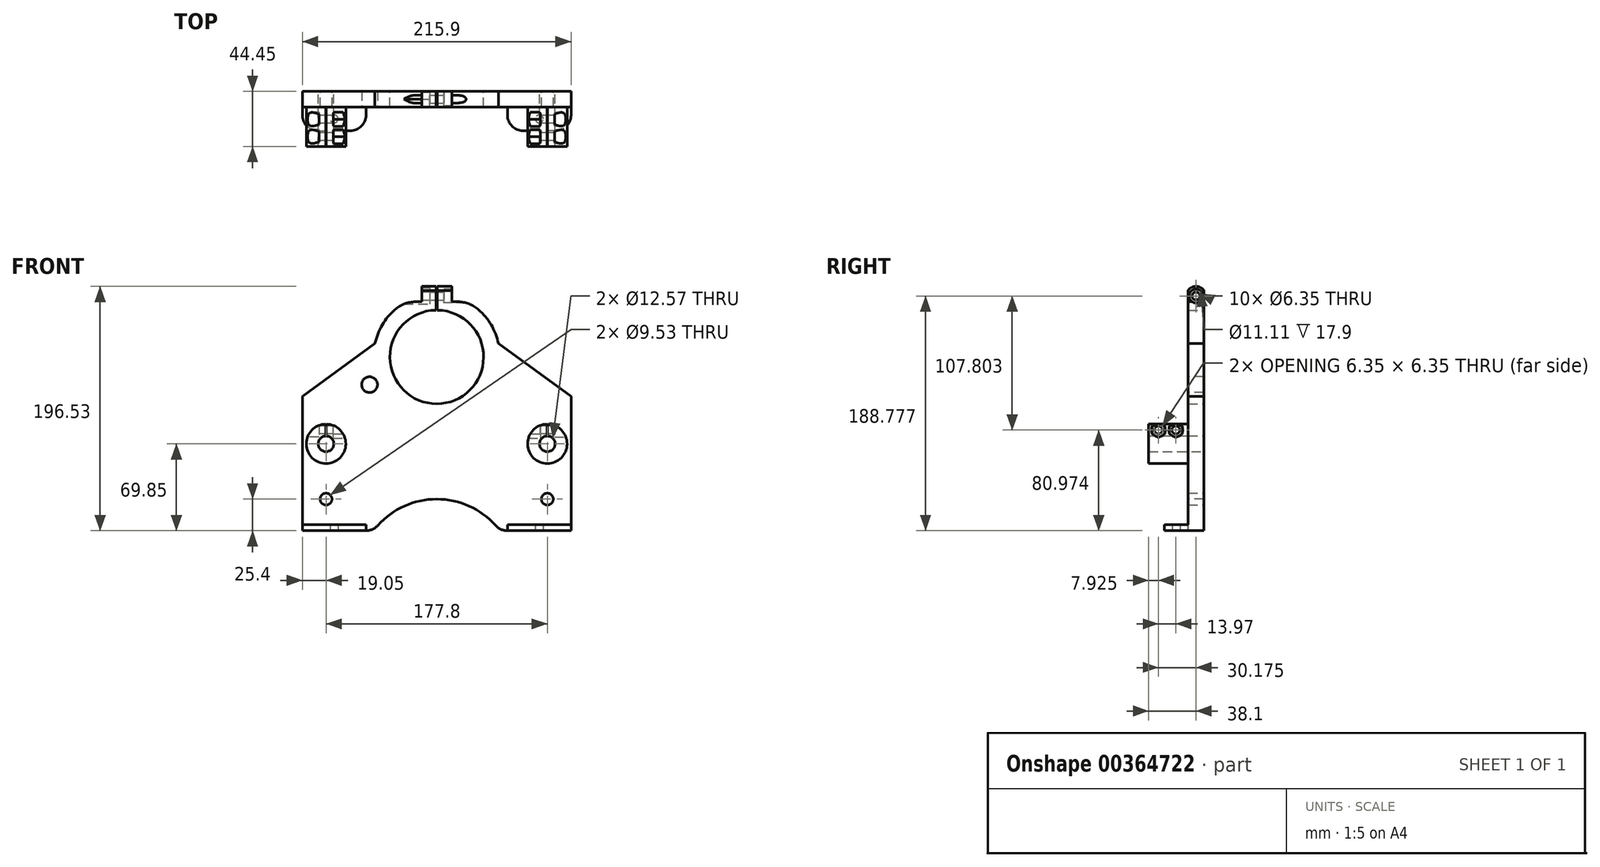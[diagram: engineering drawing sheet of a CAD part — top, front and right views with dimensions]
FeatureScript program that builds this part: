
annotation { "Feature Type Name" : "Feature", "Feature Type Description" : "" }
export const myFeature = defineFeature(function(context is Context, id is Id, definition is map)
    precondition{}
    {
        {
            var Q0;
            Q0=qCreatedBy(makeId("Front.planeOp"),FACE);
            var sketch = newSketch(context, id + "F0", { "sketchPlane" : qUnion([Q0])});
            skCircle(sketch, "E0", {"center": v(-88.9, 0) * mm, "radius": 6.29 * mm});
            skCircle(sketch, "E1", {"center": v(88.9, 0) * mm, "radius": 6.29 * mm});
            skCircle(sketch, "E2", {"center": v(-88.9, -44.45) * mm, "radius": 4.76 * mm});
            skCircle(sketch, "E3", {"center": v(88.9, -44.45) * mm, "radius": 4.76 * mm});
            skLineSegment(sketch, "E4.top", {"start": v(-107.95, -69.85) * mm, "end": v(107.95, -69.85) * mm});
            skLineSegment(sketch, "E4.left", {"start": v(-107.95, 38.1) * mm, "end": v(-107.95, -69.85) * mm});
            skLineSegment(sketch, "E4.right", {"start": v(107.95, 38.1) * mm, "end": v(107.95, -69.85) * mm});
            skPoint(sketch, "E4.middle", {"position": v(0, -15.87) * mm});
            skCircle(sketch, "E5", {"center": v(0, 69.85) * mm, "radius": 37.66 * mm});
            skArc(sketch, "E6", {"start": v(22.5, 100.6) * mm, "mid": v(0, 107.95) * mm, "end": v(-22.5, 100.6) * mm});
            skLineSegment(sketch, "E7", {"start": v(-107.95, 38.1) * mm, "end": v(-22.5, 100.6) * mm});
            skLineSegment(sketch, "E8", {"start": v(107.95, 38.1) * mm, "end": v(22.5, 100.6) * mm});
            skPoint(sketch, "E9.center.orphan", {"position": v(0, 0) * mm});
            skSolve(sketch);
        }
        {
            var Q0;
            Q0=qSketchRegion(id+"F0",true);
            extrude(context, id + "F1", {"entities" : qUnion([Q0]), "depth" : 12.7 * mm});
        }
        {
            var Q0;
            Q0=makeQuery(id+"F1.opExtrude","CAP_FACE",FACE,{"disambiguationData":[OSD([sQuery(id+"F0.wireOp",EDGE,"E9"),sQuery(id+"F0.wireOp",EDGE,"E0"),sQuery(id+"F0.wireOp",EDGE,"E1"),sQuery(id+"F0.wireOp",EDGE,"E2"),sQuery(id+"F0.wireOp",EDGE,"E3"),sQuery(id+"F0.wireOp",EDGE,"E4.bottom"),sQuery(id+"F0.wireOp",EDGE,"E4.top"),sQuery(id+"F0.wireOp",EDGE,"E4.left"),sQuery(id+"F0.wireOp",EDGE,"E4.right")])],"isStart":false});
            var sketch = newSketch(context, id + "F2", { "sketchPlane" : qUnion([Q0])});
            skCircle(sketch, "E10", {"center": v(0, -107.95) * mm, "radius": 63.5 * mm});
            skSolve(sketch);
        }
        {
            var Q0;
            Q0=qSketchRegion(id+"F2",true);
            extrude(context, id + "F3", {"entities" : qUnion([Q0]), "operationType" : NewBodyOperationType.REMOVE, "oppositeDirection" : true, "depth" : 25.4 * mm});
        }
        {
            var Q0;
            Q0=makeQuery(id+"F3.boolean.opBoolean","INTERSECT",EDGE,{"disambiguationData":[OD(0.0)],"derivedFrom":[makeQuery(id+"F1.opExtrude","SWEPT_FACE",FACE,{"disambiguationData":[OSD([sQuery(id+"F0.wireOp",EDGE,"E4.top")])]}),makeQuery(id+"F3.opExtrude","SWEPT_FACE",FACE,{"disambiguationData":[OSD([sQuery(id+"F2.wireOp",EDGE,"E10")])]})]});
            var Q1;
            Q1=makeQuery(id+"F3.boolean.opBoolean","INTERSECT",EDGE,{"disambiguationData":[OD(1.0)],"derivedFrom":[makeQuery(id+"F1.opExtrude","SWEPT_FACE",FACE,{"disambiguationData":[OSD([sQuery(id+"F0.wireOp",EDGE,"E4.top")])]}),makeQuery(id+"F3.opExtrude","SWEPT_FACE",FACE,{"disambiguationData":[OSD([sQuery(id+"F2.wireOp",EDGE,"E10")])]})]});
            fillet(context, id + "F4", {"entities" : qUnion([Q0, Q1]), "radius" : 12.7 * mm, "tangentPropagation" : true, "allowEdgeOverflow" : false});
        }
        {
            var Q0;
            Q0=makeQuery(id+"F1.opExtrude","CAP_FACE",FACE,{"disambiguationData":[OSD([sQuery(id+"F0.wireOp",EDGE,"E9"),sQuery(id+"F0.wireOp",EDGE,"E0"),sQuery(id+"F0.wireOp",EDGE,"E1"),sQuery(id+"F0.wireOp",EDGE,"E2"),sQuery(id+"F0.wireOp",EDGE,"E3"),sQuery(id+"F0.wireOp",EDGE,"E4.bottom"),sQuery(id+"F0.wireOp",EDGE,"E4.top"),sQuery(id+"F0.wireOp",EDGE,"E4.left"),sQuery(id+"F0.wireOp",EDGE,"E4.right")])],"isStart":false});
            var sketch = newSketch(context, id + "F5", { "sketchPlane" : qUnion([Q0])});
            skCircle(sketch, "E11.0", {"center": v(-88.9, 0) * mm, "radius": 6.29 * mm});
            skCircle(sketch, "E12", {"center": v(-88.9, 0) * mm, "radius": 15.88 * mm});
            skCircle(sketch, "E13.0", {"center": v(88.9, 0) * mm, "radius": 6.29 * mm});
            skCircle(sketch, "E14", {"center": v(88.9, 0) * mm, "radius": 15.88 * mm});
            skSolve(sketch);
        }
        {
            var Q0;
            Q0=qSketchRegion(id+"F5",true);
            extrude(context, id + "F6", {"entities" : qUnion([Q0]), "operationType" : NewBodyOperationType.ADD, "depth" : 31.75 * mm});
        }
        {
            var Q0;
            Q0=makeQuery(id+"F6.opExtrude","CAP_FACE",FACE,{"disambiguationData":[OSD([sQuery(id+"F5.wireOp",EDGE,"E11.0"),sQuery(id+"F5.wireOp",EDGE,"E12")])],"isStart":false});
            var sketch = newSketch(context, id + "F7", { "sketchPlane" : qUnion([Q0])});
            skLineSegment(sketch, "E15.bottom", {"start": v(-89.1, 1.72) * mm, "end": v(-88.7, 1.72) * mm});
            skLineSegment(sketch, "E15.top", {"start": v(-89.1, 19.66) * mm, "end": v(-88.7, 19.66) * mm});
            skLineSegment(sketch, "E15.left", {"start": v(-89.1, 1.72) * mm, "end": v(-89.1, 19.66) * mm});
            skLineSegment(sketch, "E15.right", {"start": v(-88.7, 1.72) * mm, "end": v(-88.7, 19.66) * mm});
            skLineSegment(sketch, "E16", {"start": v(-88.9, 1.72) * mm, "end": v(-88.9, 0) * mm});
            skPoint(sketch, "E16.endSnap0", {"position": v(-88.9, 1.72) * mm});
            skLineSegment(sketch, "E17.bottom", {"start": v(88.7, 20.83) * mm, "end": v(89.1, 20.83) * mm});
            skLineSegment(sketch, "E17.top", {"start": v(88.7, 3.08) * mm, "end": v(89.1, 3.08) * mm});
            skLineSegment(sketch, "E17.left", {"start": v(88.7, 20.83) * mm, "end": v(88.7, 3.08) * mm});
            skLineSegment(sketch, "E17.right", {"start": v(89.1, 20.83) * mm, "end": v(89.1, 3.08) * mm});
            skLineSegment(sketch, "E18", {"start": v(88.9, 0) * mm, "end": v(88.9, 3.08) * mm});
            skSolve(sketch);
        }
        {
            var Q0;
            Q0=qSketchRegion(id+"F7",true);
            var Q1;
            Q1=makeQuery(id+"F1.opExtrude","CAP_FACE",FACE,{"disambiguationData":[OSD([sQuery(id+"F0.wireOp",EDGE,"E9"),sQuery(id+"F0.wireOp",EDGE,"E0"),sQuery(id+"F0.wireOp",EDGE,"E1"),sQuery(id+"F0.wireOp",EDGE,"E2"),sQuery(id+"F0.wireOp",EDGE,"E3"),sQuery(id+"F0.wireOp",EDGE,"E4.bottom"),sQuery(id+"F0.wireOp",EDGE,"E4.top"),sQuery(id+"F0.wireOp",EDGE,"E4.left"),sQuery(id+"F0.wireOp",EDGE,"E4.right")])],"isStart":false});
            extrude(context, id + "F8", {"entities" : qUnion([Q0]), "operationType" : NewBodyOperationType.REMOVE, "endBound" : BoundingType.UP_TO_SURFACE, "oppositeDirection" : true, "endBoundEntityFace" : qUnion([Q1]), "depth" : 25.4 * mm});
        }
        {
            var Q0;
            Q0=makeQuery(id+"F1.opExtrude","SWEPT_FACE",FACE,{"disambiguationData":[OSD([sQuery(id+"F0.wireOp",EDGE,"E4.left")])]});
            var sketch = newSketch(context, id + "F9", { "sketchPlane" : qUnion([Q0])});
            skCircle(sketch, "E19", {"center": v(36.53, 11.12) * mm, "radius": 3.18 * mm});
            skCircle(sketch, "E20", {"center": v(22.56, 11.12) * mm, "radius": 3.18 * mm});
            skSolve(sketch);
        }
        {
            var Q0;
            Q0=qSketchRegion(id+"F9",true);
            extrude(context, id + "F10", {"entities" : qUnion([Q0]), "operationType" : NewBodyOperationType.REMOVE, "oppositeDirection" : true, "depth" : 224.54 * mm});
        }
        {
            var Q0;
            Q0=qCreatedBy(makeId("Right.planeOp"),FACE);
            var sketch = newSketch(context, id + "F11", { "sketchPlane" : qUnion([Q0])});
            skCircle(sketch, "E21.0", {"center": v(-36.53, 11.12) * mm, "radius": 3.18 * mm, "construction": true});
            skCircle(sketch, "E22.0", {"center": v(-22.56, 11.12) * mm, "radius": 3.18 * mm, "construction": true});
            skCircle(sketch, "E23.cCircle", {"center": v(-36.53, 11.12) * mm, "radius": 6.48 * mm, "construction": true});
            skLineSegment(sketch, "E23.0", {"start": v(-36.53, 17.6) * mm, "end": v(-30.92, 14.36) * mm});
            skLineSegment(sketch, "E23.1", {"start": v(-30.92, 14.36) * mm, "end": v(-30.92, 7.89) * mm});
            skLineSegment(sketch, "E23.2", {"start": v(-30.92, 7.89) * mm, "end": v(-36.53, 4.65) * mm});
            skLineSegment(sketch, "E23.3", {"start": v(-36.53, 4.65) * mm, "end": v(-42.13, 7.89) * mm});
            skLineSegment(sketch, "E23.4", {"start": v(-42.13, 7.89) * mm, "end": v(-42.13, 14.36) * mm});
            skLineSegment(sketch, "E23.5", {"start": v(-42.13, 14.36) * mm, "end": v(-36.53, 17.6) * mm});
            skCircle(sketch, "E24.cCircle", {"center": v(-22.56, 11.12) * mm, "radius": 6.48 * mm, "construction": true});
            skLineSegment(sketch, "E24.0", {"start": v(-28.16, 14.36) * mm, "end": v(-22.56, 17.6) * mm});
            skLineSegment(sketch, "E24.1", {"start": v(-22.56, 17.6) * mm, "end": v(-16.95, 14.36) * mm});
            skLineSegment(sketch, "E24.2", {"start": v(-16.95, 14.36) * mm, "end": v(-16.95, 7.89) * mm});
            skLineSegment(sketch, "E24.3", {"start": v(-16.95, 7.89) * mm, "end": v(-22.56, 4.65) * mm});
            skLineSegment(sketch, "E24.4", {"start": v(-22.56, 4.65) * mm, "end": v(-28.16, 7.89) * mm});
            skLineSegment(sketch, "E24.5", {"start": v(-28.16, 7.89) * mm, "end": v(-28.16, 14.36) * mm});
            skSolve(sketch);
        }
        {
            var Q0;
            Q0=makeQuery(id+"F11.imprint","IMPRINT",FACE,{"disambiguationData":[TD([[makeQuery(id+"F11.imprint","IMPRINT",EDGE,{"derivedFrom":sQuery(id+"F11.wireOp",EDGE,"E23.0")}),-1.0]])]});
            var Q1;
            Q1=makeQuery(id+"F11.imprint","IMPRINT",FACE,{"disambiguationData":[TD([[makeQuery(id+"F11.imprint","IMPRINT",EDGE,{"derivedFrom":sQuery(id+"F11.wireOp",EDGE,"E24.0")}),-1.0]])]});
            var Q2;
            Q2=sQuery(id+"F11.wireOp",EDGE,"E21.0");
            var Q3;
            Q3=sQuery(id+"F11.wireOp",EDGE,"E22.0");
            extrude(context, id + "F12", {"entities" : qUnion([Q0, Q1]), "operationType" : NewBodyOperationType.REMOVE, "surfaceEntities" : qUnion([Q2, Q3]), "oppositeDirection" : true, "depth" : 83.18 * mm, "hasSecondDirection" : true, "secondDirectionOppositeDirection" : false, "secondDirectionDepth" : 83.18 * mm});
        }
        {
            var Q0;
            Q0=makeQuery(id+"F1.opExtrude","SWEPT_FACE",FACE,{"disambiguationData":[OSD([sQuery(id+"F0.wireOp",EDGE,"E4.left")])]});
            var sketch = newSketch(context, id + "F13", { "sketchPlane" : qUnion([Q0])});
            skCircle(sketch, "E25.0", {"center": v(36.53, 11.12) * mm, "radius": 3.18 * mm, "construction": true});
            skCircle(sketch, "E26.0", {"center": v(22.56, 11.12) * mm, "radius": 3.18 * mm, "construction": true});
            skCircle(sketch, "E27", {"center": v(22.56, 11.12) * mm, "radius": 5.56 * mm});
            skCircle(sketch, "E28", {"center": v(36.53, 11.12) * mm, "radius": 5.56 * mm});
            skSolve(sketch);
        }
        {
            var Q0;
            Q0=qSketchRegion(id+"F13",true);
            extrude(context, id + "F14", {"entities" : qUnion([Q0]), "operationType" : NewBodyOperationType.REMOVE, "oppositeDirection" : true, "depth" : 13.33 * mm});
        }
        {
            var Q0;
            Q0=makeQuery(id+"F1.opExtrude","SWEPT_FACE",FACE,{"disambiguationData":[OSD([sQuery(id+"F0.wireOp",EDGE,"E4.right")])]});
            var sketch = newSketch(context, id + "F15", { "sketchPlane" : qUnion([Q0])});
            skCircle(sketch, "E29.0", {"center": v(-36.53, 11.12) * mm, "radius": 3.18 * mm, "construction": true});
            skCircle(sketch, "E29.1", {"center": v(-22.56, 11.12) * mm, "radius": 3.18 * mm, "construction": true});
            skCircle(sketch, "E30", {"center": v(-36.53, 11.12) * mm, "radius": 5.56 * mm});
            skCircle(sketch, "E31", {"center": v(-22.56, 11.12) * mm, "radius": 5.56 * mm});
            skSolve(sketch);
        }
        {
            var Q0;
            Q0=qSketchRegion(id+"F15",true);
            extrude(context, id + "F16", {"entities" : qUnion([Q0]), "operationType" : NewBodyOperationType.REMOVE, "oppositeDirection" : true, "depth" : 13.33 * mm});
        }
        {
            var Q0;
            {var subQ1=sQuery(id+"F0.wireOp",EDGE,"E4.left");var subQ2=sQuery(id+"F0.wireOp",EDGE,"E4.top");Q0=makeQuery(id+"F3.boolean.opBoolean","SPLIT",FACE,{"disambiguationData":[TD([makeQuery(id+"F1.opExtrude","SWEPT_FACE",FACE,{"disambiguationData":[OSD([subQ1])]})])],"derivedFrom":makeQuery(id+"F1.opExtrude","SWEPT_FACE",FACE,{"disambiguationData":[OSD([subQ2])]})});}
            var sketch = newSketch(context, id + "F17", { "sketchPlane" : qUnion([Q0])});
            skLineSegment(sketch, "E32.0", {"start": v(56.8, 12.7) * mm, "end": v(107.95, 12.7) * mm});
            skLineSegment(sketch, "E33", {"start": v(107.95, 12.7) * mm, "end": v(107.95, 31.75) * mm});
            skLineSegment(sketch, "E34", {"start": v(107.95, 31.75) * mm, "end": v(56.8, 31.75) * mm});
            skLineSegment(sketch, "E35", {"start": v(56.8, 31.75) * mm, "end": v(56.8, 12.7) * mm});
            skCircle(sketch, "E36", {"center": v(82.37, 22.23) * mm, "radius": 3.18 * mm});
            skLineSegment(sketch, "E37", {"start": v(107.95, 22.23) * mm, "end": v(56.8, 22.23) * mm, "construction": true});
            skLineSegment(sketch, "E38.bottom", {"start": v(-107.95, 12.7) * mm, "end": v(-56.8, 12.7) * mm});
            skLineSegment(sketch, "E38.top", {"start": v(-107.95, 31.75) * mm, "end": v(-56.8, 31.75) * mm});
            skLineSegment(sketch, "E38.left", {"start": v(-107.95, 12.7) * mm, "end": v(-107.95, 31.75) * mm});
            skLineSegment(sketch, "E38.right", {"start": v(-56.8, 12.7) * mm, "end": v(-56.8, 31.75) * mm});
            skCircle(sketch, "E39", {"center": v(-82.37, 22.22) * mm, "radius": 3.18 * mm});
            skPoint(sketch, "E39.centerSnap0", {"position": v(-82.37, 31.75) * mm});
            skSolve(sketch);
        }
        {
            var Q0;
            Q0=qSketchRegion(id+"F17",true);
            extrude(context, id + "F18", {"entities" : qUnion([Q0]), "operationType" : NewBodyOperationType.ADD, "oppositeDirection" : true, "depth" : 4.75 * mm});
        }
        {
            var Q0;
            Q0=makeQuery(id+"F18.opExtrude","SWEPT_EDGE",EDGE,{"disambiguationData":[OSD([sQuery(id+"F17.wireOp",EDGE,"E34"),sQuery(id+"F17.wireOp",EDGE,"E35")])]});
            var Q1;
            Q1=makeQuery(id+"F18.opExtrude","SWEPT_EDGE",EDGE,{"disambiguationData":[OSD([sQuery(id+"F17.wireOp",EDGE,"E33"),sQuery(id+"F17.wireOp",EDGE,"E34")])]});
            var Q2;
            Q2=makeQuery(id+"F18.opExtrude","SWEPT_EDGE",EDGE,{"disambiguationData":[OSD([sQuery(id+"F17.wireOp",EDGE,"E38.top"),sQuery(id+"F17.wireOp",EDGE,"E38.right")])]});
            var Q3;
            Q3=makeQuery(id+"F18.opExtrude","SWEPT_EDGE",EDGE,{"disambiguationData":[OSD([sQuery(id+"F17.wireOp",EDGE,"E38.top"),sQuery(id+"F17.wireOp",EDGE,"E38.left")])]});
            fillet(context, id + "F19", {"entities" : qUnion([Q0, Q1, Q2, Q3]), "radius" : 12.7 * mm, "tangentPropagation" : true, "allowEdgeOverflow" : false});
        }
        {
            var Q0;
            {var subQ0=sQuery(id+"F0.wireOp",EDGE,"E8");var subQ1=sQuery(id+"F0.wireOp",EDGE,"E7");var subQ2=sQuery(id+"F0.wireOp",EDGE,"E6");var subQ3=sQuery(id+"F0.wireOp",EDGE,"E5");var subQ4=sQuery(id+"F0.wireOp",EDGE,"E4.right");var subQ5=sQuery(id+"F0.wireOp",EDGE,"E4.left");var subQ6=sQuery(id+"F0.wireOp",EDGE,"E4.top");var subQ7=sQuery(id+"F0.wireOp",EDGE,"E3");var subQ8=sQuery(id+"F0.wireOp",EDGE,"E2");var subQ9=sQuery(id+"F0.wireOp",EDGE,"E1");var subQ10=sQuery(id+"F0.wireOp",EDGE,"E0");var subQ11=sQuery(id+"F7.wireOp",EDGE,"E15.bottom");Q0=makeQuery(id+"F8.boolean.opBoolean","MERGE",FACE,{"derivedFrom":[makeQuery(id+"F1.opExtrude","CAP_FACE",FACE,{"disambiguationData":[OSD([subQ10,subQ9,subQ8,subQ7,subQ6,subQ5,subQ4,subQ3,subQ2,subQ1,subQ0])],"isStart":false}),makeQuery(id+"F8.opExtrude","CAP_FACE",FACE,{"disambiguationData":[OSD([subQ10,subQ9,subQ8,subQ7,subQ6,subQ5,subQ4,subQ3,subQ2,subQ1,subQ0]),ownerDisambiguation([makeQuery(id+"F7.imprint","IMPRINT",EDGE,{"disambiguationData":[TD([[makeQuery(id+"F7.imprint","IMPRINT",VERTEX,{"derivedFrom":subQ11}),1.0]])],"derivedFrom":subQ11})])],"isStart":false}),makeQuery(id+"F8.opExtrude","CAP_FACE",FACE,{"disambiguationData":[OSD([subQ10,subQ9,subQ8,subQ7,subQ6,subQ5,subQ4,subQ3,subQ2,subQ1,subQ0]),ownerDisambiguation([makeQuery(id+"F7.imprint","IMPRINT",EDGE,{"derivedFrom":sQuery(id+"F7.wireOp",EDGE,"E17.bottom")})])],"isStart":false})]});}
            var sketch = newSketch(context, id + "F20", { "sketchPlane" : qUnion([Q0])});
            skCircle(sketch, "E40", {"center": v(0, 69.85) * mm, "radius": 50.8 * mm});
            skCircle(sketch, "E41.0", {"center": v(0, 69.85) * mm, "radius": 37.66 * mm});
            skSolve(sketch);
        }
        {
            var Q0;
            Q0=qSketchRegion(id+"F20",true);
            extrude(context, id + "F21", {"entities" : qUnion([Q0]), "operationType" : NewBodyOperationType.ADD, "oppositeDirection" : true, "depth" : 12.7 * mm});
        }
        {
            var Q0;
            {var subQ0=sQuery(id+"F0.wireOp",EDGE,"E8");var subQ1=sQuery(id+"F0.wireOp",EDGE,"E7");var subQ2=sQuery(id+"F0.wireOp",EDGE,"E6");var subQ3=sQuery(id+"F0.wireOp",EDGE,"E5");var subQ4=sQuery(id+"F0.wireOp",EDGE,"E4.right");var subQ5=sQuery(id+"F0.wireOp",EDGE,"E4.left");var subQ6=sQuery(id+"F0.wireOp",EDGE,"E4.top");var subQ7=sQuery(id+"F0.wireOp",EDGE,"E3");var subQ8=sQuery(id+"F0.wireOp",EDGE,"E2");var subQ9=sQuery(id+"F0.wireOp",EDGE,"E1");var subQ10=sQuery(id+"F0.wireOp",EDGE,"E0");var subQ11=sQuery(id+"F7.wireOp",EDGE,"E15.bottom");Q0=makeQuery(id+"F21.boolean.opBoolean","MERGE",FACE,{"derivedFrom":[makeQuery(id+"F8.boolean.opBoolean","MERGE",FACE,{"derivedFrom":[makeQuery(id+"F1.opExtrude","CAP_FACE",FACE,{"disambiguationData":[OSD([subQ10,subQ9,subQ8,subQ7,subQ6,subQ5,subQ4,subQ3,subQ2,subQ1,subQ0])],"isStart":false}),makeQuery(id+"F8.opExtrude","CAP_FACE",FACE,{"disambiguationData":[OSD([subQ10,subQ9,subQ8,subQ7,subQ6,subQ5,subQ4,subQ3,subQ2,subQ1,subQ0]),ownerDisambiguation([makeQuery(id+"F7.imprint","IMPRINT",EDGE,{"disambiguationData":[TD([[makeQuery(id+"F7.imprint","IMPRINT",VERTEX,{"derivedFrom":subQ11}),1.0]])],"derivedFrom":subQ11})])],"isStart":false}),makeQuery(id+"F8.opExtrude","CAP_FACE",FACE,{"disambiguationData":[OSD([subQ10,subQ9,subQ8,subQ7,subQ6,subQ5,subQ4,subQ3,subQ2,subQ1,subQ0]),ownerDisambiguation([makeQuery(id+"F7.imprint","IMPRINT",EDGE,{"derivedFrom":sQuery(id+"F7.wireOp",EDGE,"E17.bottom")})])],"isStart":false})]}),makeQuery(id+"F21.opExtrude","CAP_FACE",FACE,{"disambiguationData":[OSD([sQuery(id+"F20.wireOp",EDGE,"E40"),sQuery(id+"F20.wireOp",EDGE,"E41.0")])],"isStart":true})]});}
            var sketch = newSketch(context, id + "F22", { "sketchPlane" : qUnion([Q0])});
            skLineSegment(sketch, "E42.bottom", {"start": v(-0.8, 123.3) * mm, "end": v(0.8, 123.3) * mm});
            skLineSegment(sketch, "E42.top", {"start": v(-0.8, 97.65) * mm, "end": v(0.8, 97.65) * mm});
            skLineSegment(sketch, "E42.left", {"start": v(-0.8, 123.3) * mm, "end": v(-0.8, 97.65) * mm});
            skLineSegment(sketch, "E42.right", {"start": v(0.8, 123.3) * mm, "end": v(0.8, 97.65) * mm});
            skLineSegment(sketch, "E43", {"start": v(0, 69.85) * mm, "end": v(0, 97.65) * mm, "construction": true});
            skSolve(sketch);
        }
        {
            var Q0;
            Q0 = qSketchRegion(id + "F22", true);
            extrude(context, id + "F23", {"entities" : qUnion([Q0]), "operationType" : NewBodyOperationType.REMOVE, "oppositeDirection" : true, "depth" : 25.4 * mm});
        }
        {
            var Q0;
            {var subQ0=sQuery(id+"F0.wireOp",EDGE,"E8");var subQ1=sQuery(id+"F0.wireOp",EDGE,"E7");var subQ2=sQuery(id+"F0.wireOp",EDGE,"E6");var subQ3=sQuery(id+"F0.wireOp",EDGE,"E5");var subQ4=sQuery(id+"F0.wireOp",EDGE,"E4.right");var subQ5=sQuery(id+"F0.wireOp",EDGE,"E4.left");var subQ6=sQuery(id+"F0.wireOp",EDGE,"E4.top");var subQ7=sQuery(id+"F0.wireOp",EDGE,"E3");var subQ8=sQuery(id+"F0.wireOp",EDGE,"E2");var subQ9=sQuery(id+"F0.wireOp",EDGE,"E1");var subQ10=sQuery(id+"F0.wireOp",EDGE,"E0");var subQ11=sQuery(id+"F7.wireOp",EDGE,"E15.bottom");Q0=makeQuery(id+"F21.boolean.opBoolean","MERGE",FACE,{"derivedFrom":[makeQuery(id+"F8.boolean.opBoolean","MERGE",FACE,{"derivedFrom":[makeQuery(id+"F1.opExtrude","CAP_FACE",FACE,{"disambiguationData":[OSD([subQ10,subQ9,subQ8,subQ7,subQ6,subQ5,subQ4,subQ3,subQ2,subQ1,subQ0])],"isStart":false}),makeQuery(id+"F8.opExtrude","CAP_FACE",FACE,{"disambiguationData":[OSD([subQ10,subQ9,subQ8,subQ7,subQ6,subQ5,subQ4,subQ3,subQ2,subQ1,subQ0]),ownerDisambiguation([makeQuery(id+"F7.imprint","IMPRINT",EDGE,{"disambiguationData":[TD([[makeQuery(id+"F7.imprint","IMPRINT",VERTEX,{"derivedFrom":subQ11}),1.0]])],"derivedFrom":subQ11})])],"isStart":false}),makeQuery(id+"F8.opExtrude","CAP_FACE",FACE,{"disambiguationData":[OSD([subQ10,subQ9,subQ8,subQ7,subQ6,subQ5,subQ4,subQ3,subQ2,subQ1,subQ0]),ownerDisambiguation([makeQuery(id+"F7.imprint","IMPRINT",EDGE,{"derivedFrom":sQuery(id+"F7.wireOp",EDGE,"E17.bottom")})])],"isStart":false})]}),makeQuery(id+"F21.opExtrude","CAP_FACE",FACE,{"disambiguationData":[OSD([sQuery(id+"F20.wireOp",EDGE,"E40"),sQuery(id+"F20.wireOp",EDGE,"E41.0")])],"isStart":true})]});}
            var sketch = newSketch(context, id + "F24", { "sketchPlane" : qUnion([Q0])});
            skLineSegment(sketch, "E44.bottom", {"start": v(-6.99, 124.23) * mm, "end": v(-32.38, 124.23) * mm});
            skLineSegment(sketch, "E44.top", {"start": v(-6.98, 114.3) * mm, "end": v(-32.39, 114.3) * mm});
            skLineSegment(sketch, "E44.left", {"start": v(-6.99, 124.23) * mm, "end": v(-6.98, 114.3) * mm});
            skLineSegment(sketch, "E44.right", {"start": v(-32.39, 124.23) * mm, "end": v(-32.39, 114.3) * mm});
            skLineSegment(sketch, "E45.bottom", {"start": v(6.99, 124.23) * mm, "end": v(32.39, 124.23) * mm});
            skLineSegment(sketch, "E45.top", {"start": v(6.98, 114.3) * mm, "end": v(32.38, 114.3) * mm});
            skLineSegment(sketch, "E45.left", {"start": v(6.99, 124.23) * mm, "end": v(6.98, 114.3) * mm});
            skLineSegment(sketch, "E45.right", {"start": v(32.39, 124.23) * mm, "end": v(32.39, 114.3) * mm});
            skLineSegment(sketch, "E46", {"start": v(-6.99, 114.3) * mm, "end": v(6.98, 114.3) * mm, "construction": true});
            skLineSegment(sketch, "E47", {"start": v(0, 69.85) * mm, "end": v(0, 114.3) * mm, "construction": true});
            skSolve(sketch);
        }
        {
            var Q0;
            Q0 = qSketchRegion(id + "F24", true);
            extrude(context, id + "F25", {"entities" : qUnion([Q0]), "operationType" : NewBodyOperationType.REMOVE, "oppositeDirection" : true, "depth" : 25.4 * mm});
        }
        {
            var Q0;
            {var subQ0=sQuery(id+"F0.wireOp",EDGE,"E8");var subQ1=sQuery(id+"F0.wireOp",EDGE,"E7");var subQ2=sQuery(id+"F0.wireOp",EDGE,"E6");var subQ3=sQuery(id+"F0.wireOp",EDGE,"E5");var subQ4=sQuery(id+"F0.wireOp",EDGE,"E4.right");var subQ5=sQuery(id+"F0.wireOp",EDGE,"E4.left");var subQ6=sQuery(id+"F0.wireOp",EDGE,"E4.top");var subQ7=sQuery(id+"F0.wireOp",EDGE,"E3");var subQ8=sQuery(id+"F0.wireOp",EDGE,"E2");var subQ9=sQuery(id+"F0.wireOp",EDGE,"E1");var subQ10=sQuery(id+"F0.wireOp",EDGE,"E0");var subQ11=sQuery(id+"F7.wireOp",EDGE,"E15.bottom");Q0=makeQuery(id+"F21.boolean.opBoolean","MERGE",FACE,{"derivedFrom":[makeQuery(id+"F8.boolean.opBoolean","MERGE",FACE,{"derivedFrom":[makeQuery(id+"F1.opExtrude","CAP_FACE",FACE,{"disambiguationData":[OSD([subQ10,subQ9,subQ8,subQ7,subQ6,subQ5,subQ4,subQ3,subQ2,subQ1,subQ0])],"isStart":false}),makeQuery(id+"F8.opExtrude","CAP_FACE",FACE,{"disambiguationData":[OSD([subQ10,subQ9,subQ8,subQ7,subQ6,subQ5,subQ4,subQ3,subQ2,subQ1,subQ0]),ownerDisambiguation([makeQuery(id+"F7.imprint","IMPRINT",EDGE,{"disambiguationData":[TD([[makeQuery(id+"F7.imprint","IMPRINT",VERTEX,{"derivedFrom":subQ11}),1.0]])],"derivedFrom":subQ11})])],"isStart":false}),makeQuery(id+"F8.opExtrude","CAP_FACE",FACE,{"disambiguationData":[OSD([subQ10,subQ9,subQ8,subQ7,subQ6,subQ5,subQ4,subQ3,subQ2,subQ1,subQ0]),ownerDisambiguation([makeQuery(id+"F7.imprint","IMPRINT",EDGE,{"derivedFrom":sQuery(id+"F7.wireOp",EDGE,"E17.bottom")})])],"isStart":false})]}),makeQuery(id+"F21.opExtrude","CAP_FACE",FACE,{"disambiguationData":[OSD([sQuery(id+"F20.wireOp",EDGE,"E40"),sQuery(id+"F20.wireOp",EDGE,"E41.0")])],"isStart":true})]});}
            var sketch = newSketch(context, id + "F26", { "sketchPlane" : qUnion([Q0])});
            skLineSegment(sketch, "E48.bottom", {"start": v(-0.8, 107.5) * mm, "end": v(-6.99, 107.5) * mm});
            skLineSegment(sketch, "E48.top", {"start": v(-0.8, 123.37) * mm, "end": v(-6.99, 123.37) * mm});
            skLineSegment(sketch, "E48.left", {"start": v(-0.8, 107.5) * mm, "end": v(-0.8, 123.37) * mm});
            skLineSegment(sketch, "E48.right", {"start": v(-6.99, 107.5) * mm, "end": v(-6.99, 123.37) * mm});
            skLineSegment(sketch, "E49.bottom", {"start": v(0.8, 107.5) * mm, "end": v(6.99, 107.5) * mm});
            skLineSegment(sketch, "E49.top", {"start": v(0.8, 123.37) * mm, "end": v(6.99, 123.37) * mm});
            skLineSegment(sketch, "E49.left", {"start": v(0.8, 107.5) * mm, "end": v(0.8, 123.37) * mm});
            skLineSegment(sketch, "E49.right", {"start": v(6.99, 107.5) * mm, "end": v(6.99, 123.37) * mm});
            skSolve(sketch);
        }
        {
            var Q0;
            Q0 = qSketchRegion(id + "F26", true);
            extrude(context, id + "F27", {"entities" : qUnion([Q0]), "operationType" : NewBodyOperationType.ADD, "oppositeDirection" : true, "depth" : 12.7 * mm});
        }
        {
            var Q0;
            Q0=makeQuery(id+"F23.boolean.opBoolean","COPY",FACE,{"derivedFrom":makeQuery(id+"F23.opExtrude","SWEPT_FACE",FACE,{"disambiguationData":[OSD([sQuery(id+"F22.wireOp",EDGE,"E42.left")])]})});
            var sketch = newSketch(context, id + "F28", { "sketchPlane" : qUnion([Q0])});
            skCircle(sketch, "E50", {"center": v(-6.35, 118.93) * mm, "radius": 3.18 * mm});
            skLineSegment(sketch, "E51", {"start": v(-6.35, 118.93) * mm, "end": v(-6.35, 107.5) * mm});
            skSolve(sketch);
        }
        {
            var Q0;
            Q0 = qSketchRegion(id + "F28", true);
            extrude(context, id + "F29", {"entities" : qUnion([Q0]), "operationType" : NewBodyOperationType.REMOVE, "oppositeDirection" : true, "depth" : 25.4 * mm, "hasSecondDirection" : true, "secondDirectionOppositeDirection" : false, "secondDirectionDepth" : 25.4 * mm});
        }
        {
            var Q0;
            Q0=makeQuery(id+"F27.boolean.opBoolean","MERGE",FACE,{"derivedFrom":[makeQuery(id+"F25.boolean.opBoolean","COPY",FACE,{"derivedFrom":makeQuery(id+"F25.opExtrude","SWEPT_FACE",FACE,{"disambiguationData":[OSD([sQuery(id+"F24.wireOp",EDGE,"E45.left")])]})}),makeQuery(id+"F27.opExtrude","SWEPT_FACE",FACE,{"disambiguationData":[OSD([sQuery(id+"F26.wireOp",EDGE,"E49.right")])]})]});
            var sketch = newSketch(context, id + "F30", { "sketchPlane" : qUnion([Q0])});
            skArc(sketch, "E52", {"start": v(0, 123.37) * mm, "mid": v(-6.35, 126.68) * mm, "end": v(-12.7, 123.37) * mm});
            skLineSegment(sketch, "E53.0", {"start": v(0, 123.37) * mm, "end": v(-12.7, 123.37) * mm});
            skSolve(sketch);
        }
        {
            var Q0;
            Q0 = qSketchRegion(id + "F30", true);
            var Q1;
            Q1=makeQuery(id+"F27.boolean.opBoolean","MERGE",FACE,{"derivedFrom":[makeQuery(id+"F23.boolean.opBoolean","COPY",FACE,{"derivedFrom":makeQuery(id+"F23.opExtrude","SWEPT_FACE",FACE,{"disambiguationData":[OSD([sQuery(id+"F22.wireOp",EDGE,"E42.right")])]})}),makeQuery(id+"F27.opExtrude","SWEPT_FACE",FACE,{"disambiguationData":[OSD([sQuery(id+"F26.wireOp",EDGE,"E49.left")])]})]});
            extrude(context, id + "F31", {"entities" : qUnion([Q0]), "operationType" : NewBodyOperationType.ADD, "endBound" : BoundingType.UP_TO_SURFACE, "oppositeDirection" : true, "endBoundEntityFace" : qUnion([Q1]), "depth" : 25.4 * mm});
        }
        {
            var Q0;
            Q0=makeQuery(id+"F27.boolean.opBoolean","MERGE",FACE,{"derivedFrom":[makeQuery(id+"F25.boolean.opBoolean","COPY",FACE,{"derivedFrom":makeQuery(id+"F25.opExtrude","SWEPT_FACE",FACE,{"disambiguationData":[OSD([sQuery(id+"F24.wireOp",EDGE,"E44.left")])]})}),makeQuery(id+"F27.opExtrude","SWEPT_FACE",FACE,{"disambiguationData":[OSD([sQuery(id+"F26.wireOp",EDGE,"E48.right")])]})]});
            var sketch = newSketch(context, id + "F32", { "sketchPlane" : qUnion([Q0])});
            skArc(sketch, "E54", {"start": v(12.7, 123.37) * mm, "mid": v(6.35, 126.68) * mm, "end": v(0, 123.37) * mm});
            skLineSegment(sketch, "E55.0", {"start": v(0, 123.37) * mm, "end": v(12.7, 123.37) * mm});
            skSolve(sketch);
        }
        {
            var Q0;
            Q0 = qSketchRegion(id + "F32", true);
            var Q1;
            Q1=makeQuery(id+"F27.boolean.opBoolean","MERGE",FACE,{"derivedFrom":[makeQuery(id+"F23.boolean.opBoolean","COPY",FACE,{"derivedFrom":makeQuery(id+"F23.opExtrude","SWEPT_FACE",FACE,{"disambiguationData":[OSD([sQuery(id+"F22.wireOp",EDGE,"E42.left")])]})}),makeQuery(id+"F27.opExtrude","SWEPT_FACE",FACE,{"disambiguationData":[OSD([sQuery(id+"F26.wireOp",EDGE,"E48.left")])]})]});
            extrude(context, id + "F33", {"entities" : qUnion([Q0]), "operationType" : NewBodyOperationType.ADD, "endBound" : BoundingType.UP_TO_SURFACE, "oppositeDirection" : true, "endBoundEntityFace" : qUnion([Q1]), "depth" : 25.4 * mm});
        }
        {
            var Q0;
            {var subQ2=sQuery(id+"F0.wireOp",EDGE,"E7");var subQ13=sQuery(id+"F20.wireOp",EDGE,"E40");Q0=makeQuery(id+"F25.boolean.opBoolean","INTERSECT",EDGE,{"derivedFrom":[makeQuery(id+"F23.boolean.opBoolean","SPLIT",FACE,{"disambiguationData":[TD([makeQuery(id+"F1.opExtrude","SWEPT_FACE",FACE,{"disambiguationData":[OSD([subQ2])]})])],"derivedFrom":makeQuery(id+"F21.opExtrude","SWEPT_FACE",FACE,{"disambiguationData":[OSD([subQ13])]})}),makeQuery(id+"F25.opExtrude","SWEPT_FACE",FACE,{"disambiguationData":[OSD([sQuery(id+"F24.wireOp",EDGE,"E44.top")])]})]});}
            var Q1;
            {var subQ1=sQuery(id+"F0.wireOp",EDGE,"E8");var subQ13=sQuery(id+"F20.wireOp",EDGE,"E40");Q1=makeQuery(id+"F25.boolean.opBoolean","INTERSECT",EDGE,{"derivedFrom":[makeQuery(id+"F23.boolean.opBoolean","SPLIT",FACE,{"disambiguationData":[TD([makeQuery(id+"F1.opExtrude","SWEPT_FACE",FACE,{"disambiguationData":[OSD([subQ1])]})])],"derivedFrom":makeQuery(id+"F21.opExtrude","SWEPT_FACE",FACE,{"disambiguationData":[OSD([subQ13])]})}),makeQuery(id+"F25.opExtrude","SWEPT_FACE",FACE,{"disambiguationData":[OSD([sQuery(id+"F24.wireOp",EDGE,"E45.top")])]})]});}
            fillet(context, id + "F34", {"entities" : qUnion([Q0, Q1]), "radius" : 25.4 * mm, "tangentPropagation" : true, "allowEdgeOverflow" : false});
        }
        {
            var Q0;
            Q0=makeQuery(id+"F31.boolean.opBoolean","MERGE",FACE,{"derivedFrom":[makeQuery(id+"F27.boolean.opBoolean","MERGE",FACE,{"derivedFrom":[makeQuery(id+"F25.boolean.opBoolean","COPY",FACE,{"derivedFrom":makeQuery(id+"F25.opExtrude","SWEPT_FACE",FACE,{"disambiguationData":[OSD([sQuery(id+"F24.wireOp",EDGE,"E45.left")])]})}),makeQuery(id+"F27.opExtrude","SWEPT_FACE",FACE,{"disambiguationData":[OSD([sQuery(id+"F26.wireOp",EDGE,"E49.right")])]})]}),makeQuery(id+"F31.opExtrude","CAP_FACE",FACE,{"disambiguationData":[OSD([sQuery(id+"F30.wireOp",EDGE,"E52"),sQuery(id+"F30.wireOp",EDGE,"E53.0")])],"isStart":true})]});
            var sketch = newSketch(context, id + "F35", { "sketchPlane" : qUnion([Q0])});
            skCircle(sketch, "E56", {"center": v(-6.35, 118.93) * mm, "radius": 5.56 * mm});
            skSolve(sketch);
        }
        {
            var Q0;
            Q0 = qSketchRegion(id + "F35", true);
            extrude(context, id + "F36", {"entities" : qUnion([Q0]), "operationType" : NewBodyOperationType.REMOVE, "depth" : 28.93 * mm});
        }
        {
            var Q0;
            Q0=makeQuery(id+"F33.boolean.opBoolean","MERGE",FACE,{"derivedFrom":[makeQuery(id+"F27.boolean.opBoolean","MERGE",FACE,{"derivedFrom":[makeQuery(id+"F25.boolean.opBoolean","COPY",FACE,{"derivedFrom":makeQuery(id+"F25.opExtrude","SWEPT_FACE",FACE,{"disambiguationData":[OSD([sQuery(id+"F24.wireOp",EDGE,"E44.left")])]})}),makeQuery(id+"F27.opExtrude","SWEPT_FACE",FACE,{"disambiguationData":[OSD([sQuery(id+"F26.wireOp",EDGE,"E48.right")])]})]}),makeQuery(id+"F33.opExtrude","CAP_FACE",FACE,{"disambiguationData":[OSD([sQuery(id+"F32.wireOp",EDGE,"E54"),sQuery(id+"F32.wireOp",EDGE,"E55.0")])],"isStart":true})]});
            var sketch = newSketch(context, id + "F37", { "sketchPlane" : qUnion([Q0])});
            skCircle(sketch, "E57.cCircle", {"center": v(6.35, 118.93) * mm, "radius": 6.48 * mm, "construction": true});
            skLineSegment(sketch, "E57.0", {"start": v(0.74, 122.17) * mm, "end": v(6.35, 125.4) * mm});
            skLineSegment(sketch, "E57.1", {"start": v(6.35, 125.4) * mm, "end": v(11.96, 122.17) * mm});
            skLineSegment(sketch, "E57.2", {"start": v(11.96, 122.17) * mm, "end": v(11.96, 115.69) * mm});
            skLineSegment(sketch, "E57.3", {"start": v(11.96, 115.69) * mm, "end": v(6.35, 112.45) * mm});
            skLineSegment(sketch, "E57.4", {"start": v(6.35, 112.45) * mm, "end": v(0.74, 115.69) * mm});
            skLineSegment(sketch, "E57.5", {"start": v(0.74, 115.69) * mm, "end": v(0.74, 122.17) * mm});
            skSolve(sketch);
        }
        {
            var Q0;
            Q0 = qSketchRegion(id + "F37", true);
            extrude(context, id + "F38", {"entities" : qUnion([Q0]), "operationType" : NewBodyOperationType.REMOVE, "depth" : 22.22 * mm});
        }
        {
            var Q0;
            {var subQ0=sQuery(id+"F0.wireOp",EDGE,"E8");var subQ1=sQuery(id+"F0.wireOp",EDGE,"E7");var subQ2=sQuery(id+"F0.wireOp",EDGE,"E6");var subQ3=sQuery(id+"F0.wireOp",EDGE,"E5");var subQ4=sQuery(id+"F0.wireOp",EDGE,"E4.right");var subQ5=sQuery(id+"F0.wireOp",EDGE,"E4.left");var subQ6=sQuery(id+"F0.wireOp",EDGE,"E4.top");var subQ7=sQuery(id+"F0.wireOp",EDGE,"E3");var subQ8=sQuery(id+"F0.wireOp",EDGE,"E2");var subQ9=sQuery(id+"F0.wireOp",EDGE,"E1");var subQ10=sQuery(id+"F0.wireOp",EDGE,"E0");var subQ11=sQuery(id+"F7.wireOp",EDGE,"E15.bottom");Q0=makeQuery(id+"F27.boolean.opBoolean","MERGE",FACE,{"derivedFrom":[makeQuery(id+"F21.boolean.opBoolean","MERGE",FACE,{"derivedFrom":[makeQuery(id+"F8.boolean.opBoolean","MERGE",FACE,{"derivedFrom":[makeQuery(id+"F1.opExtrude","CAP_FACE",FACE,{"disambiguationData":[OSD([subQ10,subQ9,subQ8,subQ7,subQ6,subQ5,subQ4,subQ3,subQ2,subQ1,subQ0])],"isStart":false}),makeQuery(id+"F8.opExtrude","CAP_FACE",FACE,{"disambiguationData":[OSD([subQ10,subQ9,subQ8,subQ7,subQ6,subQ5,subQ4,subQ3,subQ2,subQ1,subQ0]),ownerDisambiguation([makeQuery(id+"F7.imprint","IMPRINT",EDGE,{"disambiguationData":[TD([[makeQuery(id+"F7.imprint","IMPRINT",VERTEX,{"derivedFrom":subQ11}),1.0]])],"derivedFrom":subQ11})])],"isStart":false}),makeQuery(id+"F8.opExtrude","CAP_FACE",FACE,{"disambiguationData":[OSD([subQ10,subQ9,subQ8,subQ7,subQ6,subQ5,subQ4,subQ3,subQ2,subQ1,subQ0]),ownerDisambiguation([makeQuery(id+"F7.imprint","IMPRINT",EDGE,{"derivedFrom":sQuery(id+"F7.wireOp",EDGE,"E17.bottom")})])],"isStart":false})]}),makeQuery(id+"F21.opExtrude","CAP_FACE",FACE,{"disambiguationData":[OSD([sQuery(id+"F20.wireOp",EDGE,"E40"),sQuery(id+"F20.wireOp",EDGE,"E41.0")])],"isStart":true})]}),makeQuery(id+"F27.opExtrude","CAP_FACE",FACE,{"disambiguationData":[OSD([sQuery(id+"F26.wireOp",EDGE,"E48.bottom"),sQuery(id+"F26.wireOp",EDGE,"E48.top"),sQuery(id+"F26.wireOp",EDGE,"E48.left"),sQuery(id+"F26.wireOp",EDGE,"E48.right")])],"isStart":true}),makeQuery(id+"F27.opExtrude","CAP_FACE",FACE,{"disambiguationData":[OSD([sQuery(id+"F26.wireOp",EDGE,"E49.bottom"),sQuery(id+"F26.wireOp",EDGE,"E49.top"),sQuery(id+"F26.wireOp",EDGE,"E49.left"),sQuery(id+"F26.wireOp",EDGE,"E49.right")])],"isStart":true})]});}
            var sketch = newSketch(context, id + "F39", { "sketchPlane" : qUnion([Q0])});
            skCircle(sketch, "E58", {"center": v(-53.98, 47.63) * mm, "radius": 6.35 * mm});
            skSolve(sketch);
        }
        {
            var Q0;
            Q0 = qSketchRegion(id + "F39", true);
            extrude(context, id + "F40", {"entities" : qUnion([Q0]), "operationType" : NewBodyOperationType.REMOVE, "oppositeDirection" : true, "depth" : 25.4 * mm});
        }
        {
            var Q0;
            Q0=makeQuery(id+"F36.boolean.opBoolean","MERGE",FACE,{"derivedFrom":[makeQuery(id+"F31.boolean.opBoolean","MERGE",FACE,{"derivedFrom":[makeQuery(id+"F27.boolean.opBoolean","MERGE",FACE,{"derivedFrom":[makeQuery(id+"F25.boolean.opBoolean","COPY",FACE,{"derivedFrom":makeQuery(id+"F25.opExtrude","SWEPT_FACE",FACE,{"disambiguationData":[OSD([sQuery(id+"F24.wireOp",EDGE,"E45.left")])]})}),makeQuery(id+"F27.opExtrude","SWEPT_FACE",FACE,{"disambiguationData":[OSD([sQuery(id+"F26.wireOp",EDGE,"E49.right")])]})]}),makeQuery(id+"F31.opExtrude","CAP_FACE",FACE,{"disambiguationData":[OSD([sQuery(id+"F30.wireOp",EDGE,"E52"),sQuery(id+"F30.wireOp",EDGE,"E53.0")])],"isStart":true})]}),makeQuery(id+"F36.opExtrude","CAP_FACE",FACE,{"disambiguationData":[OSD([sQuery(id+"F35.wireOp",EDGE,"E56")])],"isStart":true})]});
            extrude(context, id + "F41", {"entities" : qUnion([Q0]), "operationType" : NewBodyOperationType.REMOVE, "oppositeDirection" : true, "depth" : 1.27 * mm});
        }
        {
            var Q0;
            Q0=makeQuery(id+"F38.boolean.opBoolean","MERGE",FACE,{"derivedFrom":[makeQuery(id+"F33.boolean.opBoolean","MERGE",FACE,{"derivedFrom":[makeQuery(id+"F27.boolean.opBoolean","MERGE",FACE,{"derivedFrom":[makeQuery(id+"F25.boolean.opBoolean","COPY",FACE,{"derivedFrom":makeQuery(id+"F25.opExtrude","SWEPT_FACE",FACE,{"disambiguationData":[OSD([sQuery(id+"F24.wireOp",EDGE,"E44.left")])]})}),makeQuery(id+"F27.opExtrude","SWEPT_FACE",FACE,{"disambiguationData":[OSD([sQuery(id+"F26.wireOp",EDGE,"E48.right")])]})]}),makeQuery(id+"F33.opExtrude","CAP_FACE",FACE,{"disambiguationData":[OSD([sQuery(id+"F32.wireOp",EDGE,"E54"),sQuery(id+"F32.wireOp",EDGE,"E55.0")])],"isStart":true})]}),makeQuery(id+"F38.opExtrude","CAP_FACE",FACE,{"disambiguationData":[OSD([sQuery(id+"F37.wireOp",EDGE,"E57.0"),sQuery(id+"F37.wireOp",EDGE,"E57.1"),sQuery(id+"F37.wireOp",EDGE,"E57.2"),sQuery(id+"F37.wireOp",EDGE,"E57.3"),sQuery(id+"F37.wireOp",EDGE,"E57.4"),sQuery(id+"F37.wireOp",EDGE,"E57.5")])],"isStart":true})]});
            extrude(context, id + "F42", {"entities" : qUnion([Q0]), "operationType" : NewBodyOperationType.REMOVE, "oppositeDirection" : true, "depth" : 1.27 * mm});
        }
        {
            var Q0;
            Q0=makeQuery(id+"F41.boolean.opBoolean","COPY",FACE,{"derivedFrom":makeQuery(id+"F41.opExtrude","CAP_FACE",FACE,{"disambiguationData":[OSD([sQuery(id+"F24.wireOp",EDGE,"E45.left"),sQuery(id+"F26.wireOp",EDGE,"E49.right"),sQuery(id+"F30.wireOp",EDGE,"E52"),sQuery(id+"F30.wireOp",EDGE,"E53.0"),sQuery(id+"F35.wireOp",EDGE,"E56")])],"isStart":false})});
            var sketch = newSketch(context, id + "F43", { "sketchPlane" : qUnion([Q0])});
            skLineSegment(sketch, "E59.0", {"start": v(0, 114.3) * mm, "end": v(-3.27, 114.3) * mm});
            skLineSegment(sketch, "E59.1", {"start": v(0, 123.37) * mm, "end": v(0, 114.3) * mm});
            skLineSegment(sketch, "E59.2", {"start": v(-12.7, 123.37) * mm, "end": v(-12.7, 114.3) * mm});
            skLineSegment(sketch, "E59.3", {"start": v(-9.43, 114.3) * mm, "end": v(-12.7, 114.3) * mm});
            skArc(sketch, "E59.4", {"start": v(0, 123.37) * mm, "mid": v(-6.35, 126.68) * mm, "end": v(-12.7, 123.37) * mm});
            skArc(sketch, "E60", {"start": v(-3.27, 114.3) * mm, "mid": v(-6.35, 124.48) * mm, "end": v(-9.43, 114.3) * mm});
            skSolve(sketch);
        }
        {
            var Q0;
            Q0 = qSketchRegion(id + "F43", true);
            extrude(context, id + "F44", {"entities" : qUnion([Q0]), "operationType" : NewBodyOperationType.ADD, "depth" : 6.35 * mm});
        }
        {
            var Q0;
            Q0=makeQuery(id+"F42.boolean.opBoolean","COPY",FACE,{"derivedFrom":makeQuery(id+"F42.opExtrude","CAP_FACE",FACE,{"disambiguationData":[OSD([sQuery(id+"F24.wireOp",EDGE,"E44.left"),sQuery(id+"F26.wireOp",EDGE,"E48.right"),sQuery(id+"F32.wireOp",EDGE,"E54"),sQuery(id+"F32.wireOp",EDGE,"E55.0"),sQuery(id+"F37.wireOp",EDGE,"E57.0"),sQuery(id+"F37.wireOp",EDGE,"E57.1"),sQuery(id+"F37.wireOp",EDGE,"E57.2"),sQuery(id+"F37.wireOp",EDGE,"E57.3"),sQuery(id+"F37.wireOp",EDGE,"E57.4"),sQuery(id+"F37.wireOp",EDGE,"E57.5")])],"isStart":false})});
            var sketch = newSketch(context, id + "F45", { "sketchPlane" : qUnion([Q0])});
            skCircle(sketch, "E61.cCircle", {"center": v(6.35, 118.93) * mm, "radius": 6.48 * mm, "construction": true});
            skLineSegment(sketch, "E61.0", {"start": v(3.15, 114.3) * mm, "end": v(0.74, 115.69) * mm});
            skLineSegment(sketch, "E61.1", {"start": v(0.74, 115.69) * mm, "end": v(0.74, 122.17) * mm});
            skLineSegment(sketch, "E61.2", {"start": v(0.74, 122.17) * mm, "end": v(6.35, 125.4) * mm});
            skLineSegment(sketch, "E61.3", {"start": v(6.35, 125.4) * mm, "end": v(11.96, 122.17) * mm});
            skLineSegment(sketch, "E61.4", {"start": v(11.96, 122.17) * mm, "end": v(11.96, 115.69) * mm});
            skLineSegment(sketch, "E61.5", {"start": v(11.96, 115.69) * mm, "end": v(9.55, 114.3) * mm});
            skArc(sketch, "E62.0", {"start": v(12.7, 123.37) * mm, "mid": v(6.35, 126.68) * mm, "end": v(0, 123.37) * mm});
            skLineSegment(sketch, "E63.0", {"start": v(12.7, 123.37) * mm, "end": v(12.7, 114.3) * mm});
            skLineSegment(sketch, "E64.0", {"start": v(0, 123.37) * mm, "end": v(0, 114.3) * mm});
            skLineSegment(sketch, "E65.0", {"start": v(9.55, 114.3) * mm, "end": v(12.7, 114.3) * mm});
            skLineSegment(sketch, "E66.0", {"start": v(0, 114.3) * mm, "end": v(3.15, 114.3) * mm});
            skPoint(sketch, "E67.orphan", {"position": v(6.35, 112.45) * mm});
            skSolve(sketch);
        }
        {
            var Q0;
            Q0 = qSketchRegion(id + "F45", true);
            extrude(context, id + "F46", {"entities" : qUnion([Q0]), "operationType" : NewBodyOperationType.ADD, "depth" : 6.35 * mm});
        }
        {
            var Q0;
            {var subQ0=sQuery(id+"F26.wireOp",EDGE,"E48.left");var subQ1=sQuery(id+"F22.wireOp",EDGE,"E42.left");Q0=makeQuery(id+"F33.boolean.opBoolean","MERGE",FACE,{"derivedFrom":[makeQuery(id+"F27.boolean.opBoolean","MERGE",FACE,{"derivedFrom":[makeQuery(id+"F23.boolean.opBoolean","COPY",FACE,{"derivedFrom":makeQuery(id+"F23.opExtrude","SWEPT_FACE",FACE,{"disambiguationData":[OSD([subQ1])]})}),makeQuery(id+"F27.opExtrude","SWEPT_FACE",FACE,{"disambiguationData":[OSD([subQ0])]})]}),makeQuery(id+"F33.opExtrude","CAP_FACE",FACE,{"disambiguationData":[OSD([subQ1,subQ0])],"isStart":false})]});}
            extrude(context, id + "F47", {"entities" : qUnion([Q0]), "operationType" : NewBodyOperationType.ADD, "depth" : 0.25 * mm, "offsetDistance" : 25.4 * mm});
        }
        {
            var Q0;
            {var subQ0=sQuery(id+"F26.wireOp",EDGE,"E49.left");var subQ1=sQuery(id+"F22.wireOp",EDGE,"E42.right");Q0=makeQuery(id+"F31.boolean.opBoolean","MERGE",FACE,{"derivedFrom":[makeQuery(id+"F27.boolean.opBoolean","MERGE",FACE,{"derivedFrom":[makeQuery(id+"F23.boolean.opBoolean","COPY",FACE,{"derivedFrom":makeQuery(id+"F23.opExtrude","SWEPT_FACE",FACE,{"disambiguationData":[OSD([subQ1])]})}),makeQuery(id+"F27.opExtrude","SWEPT_FACE",FACE,{"disambiguationData":[OSD([subQ0])]})]}),makeQuery(id+"F31.opExtrude","CAP_FACE",FACE,{"disambiguationData":[OSD([subQ1,subQ0])],"isStart":false})]});}
            extrude(context, id + "F48", {"entities" : qUnion([Q0]), "operationType" : NewBodyOperationType.ADD, "depth" : 0.25 * mm, "offsetDistance" : 25.4 * mm});
        }
    });
